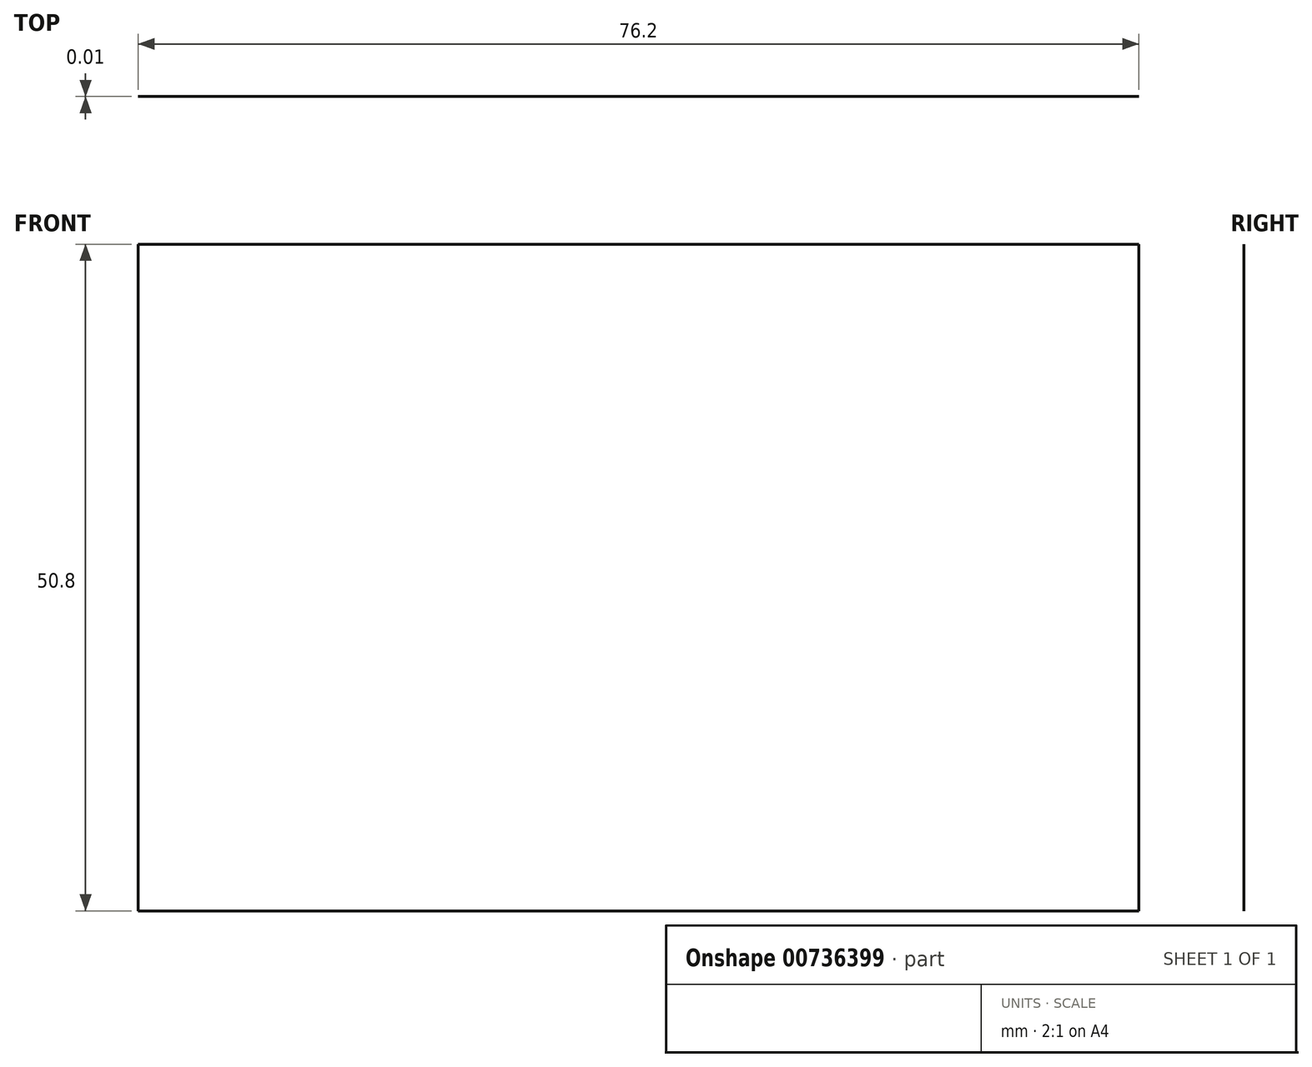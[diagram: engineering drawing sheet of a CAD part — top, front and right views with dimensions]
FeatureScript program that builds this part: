
annotation { "Feature Type Name" : "Feature", "Feature Type Description" : "" }
export const myFeature = defineFeature(function(context is Context, id is Id, definition is map)
    precondition{}
    {
        {
            var Q0;
            Q0=qCreatedBy(makeId("Front.planeOp"),FACE);
            var sketch = newSketch(context, id + "F0", { "sketchPlane" : qUnion([Q0])});
            skLineSegment(sketch, "E0.bottom", {"start": v(0, 0) * mm, "end": v(76.2, 0) * mm});
            skLineSegment(sketch, "E0.top", {"start": v(0, 50.8) * mm, "end": v(76.2, 50.8) * mm});
            skLineSegment(sketch, "E0.left", {"start": v(0, 0) * mm, "end": v(0, 50.8) * mm});
            skLineSegment(sketch, "E0.right", {"start": v(76.2, 0) * mm, "end": v(76.2, 50.8) * mm});
            skSolve(sketch);
        }
        {
            var Q0;
            Q0=makeQuery(id+"F0.imprint","IMPRINT",FACE,{"disambiguationData":[TD([[makeQuery(id+"F0.imprint","IMPRINT",EDGE,{"derivedFrom":sQuery(id+"F0.wireOp",EDGE,"E0.bottom")}),1.0]])]});
            extrude(context, id + "F1", {"entities" : qUnion([Q0]), "depth" : 3 / 406.4 * mm, "offsetDistance" : 25.4 * mm});
        }
    });
